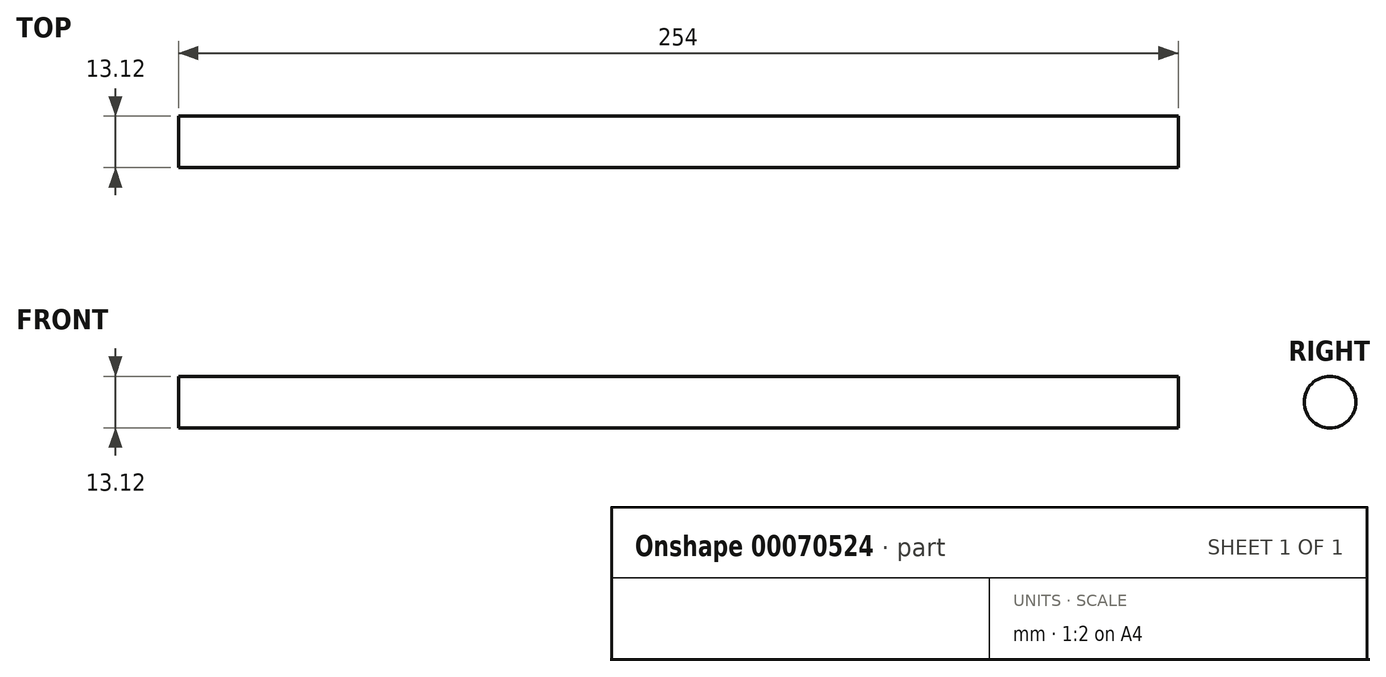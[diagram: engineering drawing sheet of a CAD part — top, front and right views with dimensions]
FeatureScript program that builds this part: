
annotation { "Feature Type Name" : "Feature", "Feature Type Description" : "" }
export const myFeature = defineFeature(function(context is Context, id is Id, definition is map)
    precondition{}
    {
        {
            var Q0;
            Q0=qCreatedBy(makeId("Right.planeOp"),FACE);
            var sketch = newSketch(context, id + "F0", { "sketchPlane" : qUnion([Q0])});
            skCircle(sketch, "E0", {"center": v(0, 0) * mm, "radius": 6.56 * mm});
            skSolve(sketch);
        }
        {
            var Q0;
            Q0 = qSketchRegion(id + "F0", true);
            extrude(context, id + "F1", {"entities" : qUnion([Q0]), "endBound" : BoundingType.SYMMETRIC, "depth" : 254 * mm});
        }
    });
